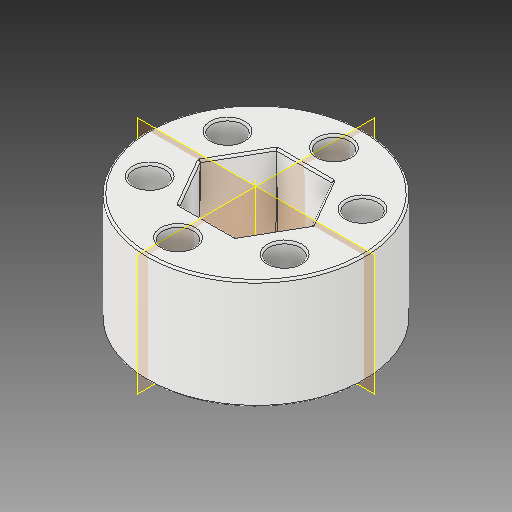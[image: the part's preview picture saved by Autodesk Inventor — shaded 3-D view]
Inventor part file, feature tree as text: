
AUTODESK INVENTOR PART (.ipt)
format: ipt  version: 2018 (Build 220112000, 112)  size: 270,336 bytes
history: native  units: in
note: dims shown in document units (in); Inventor stores cm internally (conversion verified against a paired STEP export)
features: plane x1, other x1, fillet x1
ambient origin geometry x8: Origin, YZ Plane, XZ Plane, XY Plane, X Axis, Y Axis, Z Axis, Center Point
bodies: Solid1 (feature_tree)
feature tree (3):
  plane  "Work Plane1"
  other  "Work Axis1"
  fillet  "Fillet2"  Radius=0.6184in
